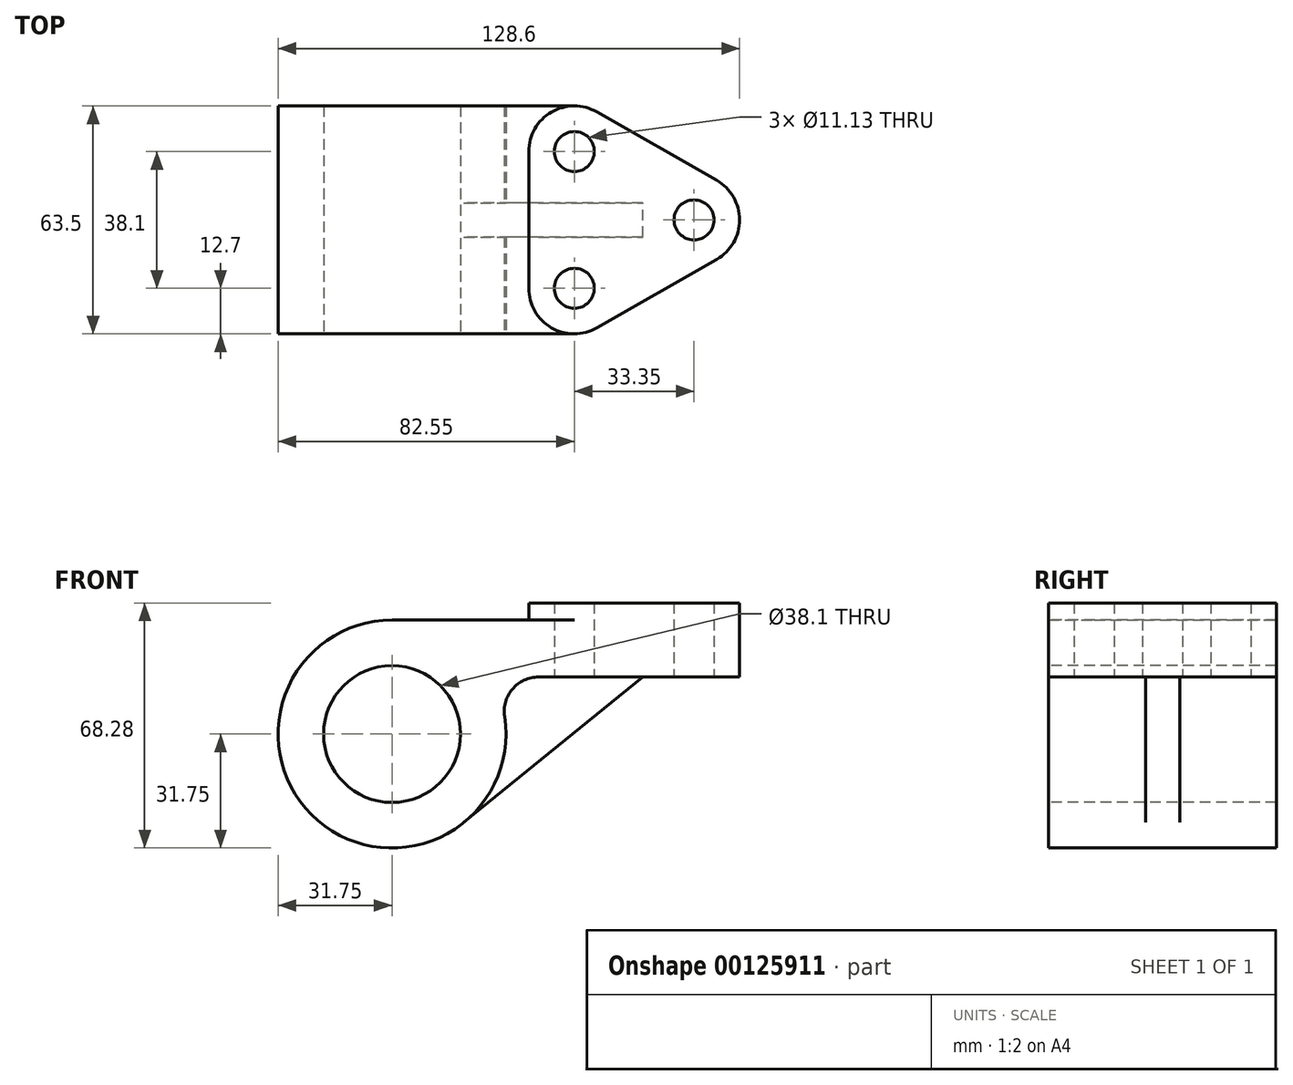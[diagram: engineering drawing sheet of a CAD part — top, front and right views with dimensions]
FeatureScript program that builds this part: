
annotation { "Feature Type Name" : "Feature", "Feature Type Description" : "" }
export const myFeature = defineFeature(function(context is Context, id is Id, definition is map)
    precondition{}
    {
        {
            var Q0;
            Q0=qCreatedBy(makeId("Front.planeOp"),FACE);
            var sketch = newSketch(context, id + "F0", { "sketchPlane" : qUnion([Q0])});
            skCircle(sketch, "E0", {"center": v(0, 0) * mm, "radius": 19.05 * mm});
            skCircle(sketch, "E1", {"center": v(0, 0) * mm, "radius": 31.75 * mm});
            skLineSegment(sketch, "E2", {"start": v(0, 31.75) * mm, "end": v(50.8, 31.75) * mm});
            skLineSegment(sketch, "E3", {"start": v(50.8, 31.75) * mm, "end": v(50.8, 15.87) * mm});
            skLineSegment(sketch, "E4", {"start": v(50.8, 15.87) * mm, "end": v(27.5, 15.87) * mm});
            skSolve(sketch);
        }
        {
            var Q0;
            Q0 = qSketchRegion(id + "F0", true);
            extrude(context, id + "F1", {"entities" : qUnion([Q0]), "endBound" : BoundingType.SYMMETRIC, "oppositeDirection" : true, "depth" : 63.5 * mm});
        }
        {
            var Q0;
            Q0=makeQuery(id+"F1.opExtrude","SWEPT_FACE",FACE,{"disambiguationData":[OSD([sQuery(id+"F0.wireOp",EDGE,"E4")])]});
            var sketch = newSketch(context, id + "F2", { "sketchPlane" : qUnion([Q0])});
            skCircle(sketch, "E5", {"center": v(50.8, 19.05) * mm, "radius": 5.56 * mm});
            skCircle(sketch, "E6", {"center": v(50.8, -19.05) * mm, "radius": 5.56 * mm});
            skCircle(sketch, "E7", {"center": v(84.15, 0) * mm, "radius": 5.56 * mm});
            skLineSegment(sketch, "E8", {"start": v(50.8, 31.75) * mm, "end": v(27.5, 31.75) * mm, "construction": true});
            skLineSegment(sketch, "E9", {"start": v(27.5, 31.75) * mm, "end": v(27.5, -31.75) * mm, "construction": true});
            skLineSegment(sketch, "E10", {"start": v(27.5, -31.75) * mm, "end": v(50.8, -31.75) * mm, "construction": true});
            skLineSegment(sketch, "E11", {"start": v(50.8, -31.75) * mm, "end": v(50.8, 31.75) * mm, "construction": true});
            skArc(sketch, "E12", {"start": v(57.1, 30.08) * mm, "mid": v(44.42, 30.03) * mm, "end": v(38.1, 19.05) * mm});
            skArc(sketch, "E13", {"start": v(90.45, -11.03) * mm, "mid": v(96.85, 0) * mm, "end": v(90.45, 11.03) * mm});
            skArc(sketch, "E14", {"start": v(38.1, -19.05) * mm, "mid": v(44.42, -30.03) * mm, "end": v(57.1, -30.08) * mm});
            skLineSegment(sketch, "E15", {"start": v(57.1, 30.08) * mm, "end": v(90.45, 11.03) * mm});
            skLineSegment(sketch, "E16", {"start": v(90.45, -11.03) * mm, "end": v(57.1, -30.08) * mm});
            skLineSegment(sketch, "E17", {"start": v(38.1, 19.05) * mm, "end": v(38.1, -19.05) * mm});
            skSolve(sketch);
        }
        {
            var Q0;
            Q0 = qSketchRegion(id + "F2", true);
            extrude(context, id + "F3", {"entities" : qUnion([Q0]), "operationType" : NewBodyOperationType.ADD, "oppositeDirection" : true, "depth" : 20.65 * mm});
        }
        {
            var Q0;
            Q0=makeQuery(id+"F1.opExtrude","SWEPT_EDGE",EDGE,{"disambiguationData":[OSD([sQuery(id+"F0.wireOp",EDGE,"E1"),sQuery(id+"F0.wireOp",EDGE,"E4")])]});
            fillet(context, id + "F4", {"entities" : qUnion([Q0]), "radius" : 9.52 * mm, "tangentPropagation" : true, "allowEdgeOverflow" : false});
        }
        {
            var Q0;
            Q0=qCreatedBy(makeId("Front.planeOp"),FACE);
            var sketch = newSketch(context, id + "F5", { "sketchPlane" : qUnion([Q0])});
            skLineSegment(sketch, "E18", {"start": v(69.85, 15.88) * mm, "end": v(20.03, -24.63) * mm});
            skArc(sketch, "E19.0", {"start": v(20.03, -24.63) * mm, "mid": v(29.64, -11.39) * mm, "end": v(31.37, 4.88) * mm});
            skArc(sketch, "E19.1", {"start": v(31.37, 4.88) * mm, "mid": v(33.55, 12.55) * mm, "end": v(40.78, 15.87) * mm});
            skLineSegment(sketch, "E19.2", {"start": v(50.8, 15.87) * mm, "end": v(40.78, 15.87) * mm});
            skLineSegment(sketch, "E19.3", {"start": v(57.1, 15.88) * mm, "end": v(50.8, 15.88) * mm});
            skLineSegment(sketch, "E19.4", {"start": v(57.1, 15.88) * mm, "end": v(69.85, 15.88) * mm});
            skPoint(sketch, "E20", {"position": v(20.03, -24.63) * mm});
            skPoint(sketch, "E21", {"position": v(69.85, 15.88) * mm});
            skPoint(sketch, "E22.orphan", {"position": v(0, 31.75) * mm});
            skPoint(sketch, "E23.orphan", {"position": v(90.45, 15.88) * mm});
            skSolve(sketch);
        }
        {
            var Q0;
            Q0 = qSketchRegion(id + "F5", true);
            extrude(context, id + "F6", {"entities" : qUnion([Q0]), "operationType" : NewBodyOperationType.ADD, "endBound" : BoundingType.SYMMETRIC, "depth" : 9.52 * mm});
        }
        {
            var Q0;
            Q0=makeQuery(id+"F3.opExtrude","CAP_FACE",FACE,{"disambiguationData":[OSD([sQuery(id+"F2.wireOp",EDGE,"E5"),sQuery(id+"F2.wireOp",EDGE,"E6"),sQuery(id+"F2.wireOp",EDGE,"E7"),sQuery(id+"F2.wireOp",EDGE,"E12"),sQuery(id+"F2.wireOp",EDGE,"E13"),sQuery(id+"F2.wireOp",EDGE,"E14"),sQuery(id+"F2.wireOp",EDGE,"E15"),sQuery(id+"F2.wireOp",EDGE,"E16"),sQuery(id+"F2.wireOp",EDGE,"E17")])],"isStart":false});
            var sketch = newSketch(context, id + "F7", { "sketchPlane" : qUnion([Q0])});
            skCircle(sketch, "E24.0", {"center": v(50.8, 19.05) * mm, "radius": 5.56 * mm});
            skCircle(sketch, "E25.0", {"center": v(50.8, -19.05) * mm, "radius": 5.56 * mm});
            skSolve(sketch);
        }
        {
            var Q0;
            Q0 = qSketchRegion(id + "F7", true);
            extrude(context, id + "F8", {"entities" : qUnion([Q0]), "operationType" : NewBodyOperationType.REMOVE, "endBound" : BoundingType.THROUGH_ALL, "oppositeDirection" : true, "depth" : 25.4 * mm});
        }
    });
